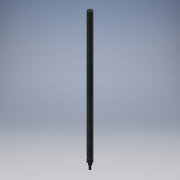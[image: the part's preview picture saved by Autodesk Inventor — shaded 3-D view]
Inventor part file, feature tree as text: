
AUTODESK INVENTOR PART (.ipt)
format: ipt  version: 2016 (Build 200138000, 138)  size: 147,456 bytes
history: native  units: in
note: dims shown in document units (in); Inventor stores cm internally (conversion verified against a paired STEP export)
features: extrude x1, sketch x1, imported_body x1
ambient origin geometry x8: Origin, YZ Plane, XZ Plane, XY Plane, X Axis, Y Axis, Z Axis, Center Point
bodies: Solid1 (feature_tree)
feature tree (3):
  extrude  "Extrusion1"  Depth=13.0in TaperAngle=0.0deg
  sketch  "Sketch1"  dims[d0=0.5in d1=13.0in d2=0.0in]
  imported_body  "Imported1"
